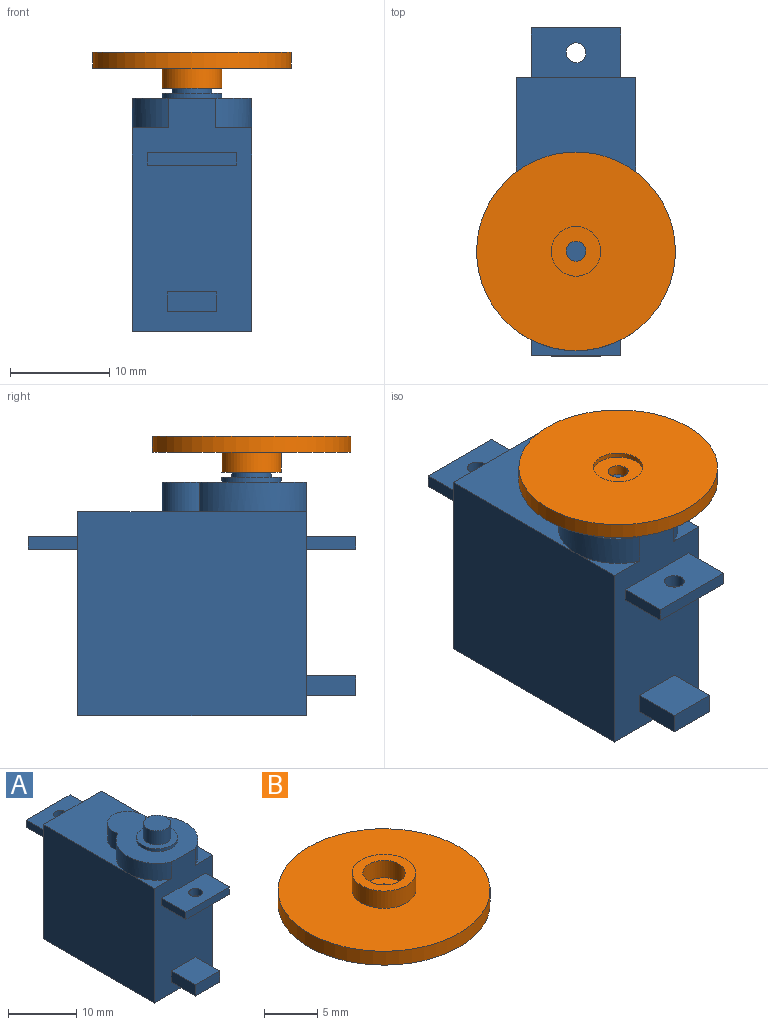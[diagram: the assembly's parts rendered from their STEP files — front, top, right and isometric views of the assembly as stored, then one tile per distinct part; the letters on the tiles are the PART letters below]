
ASSEMBLY  parts=2 mates=1
PART A: 33 faces, bbox 12x33x26.5 mm
  f0: plane 23.5x12mm, normal (0,-1,0), area 238.7mm2, adj f1,f2,f3,f4,f7,f8,f10,f11
  f1: plane 5.5x3.6mm, normal (0,0,1), area 5.5mm2, adj f0,f3,f10
  f2: plane 5.5x3.6mm, normal (0,0,1), area 5.5mm2, adj f0,f4,f8
  f3: plane 23x20.5mm, normal (-1,0,0), area 471.5mm2, adj f0,f1,f5,f6,f7
  f4: plane 23x20.5mm, normal (1,0,0), area 471.5mm2, adj f0,f2,f5,f6,f7
  f5: plane 20.5x12mm, normal (0,1,0), area 234.3mm2, adj f3,f4,f6,f7,f22,f24,f26,f27
  f6: plane 17.5x12mm, normal (0,0,1), area 137.8mm2, adj f3,f4,f5,f8,f9,f10
  f7: plane 23x12mm, normal (0,0,-1), area 276mm2, adj f0,f3,f4,f5
  f8: cylinder r=6mm len=10.75mm, axis (0,0,-1), area 40.1mm2, adj f0,f2,f6,f9,f11
  f9: cylinder r=3mm len=6mm, axis (0,0,-1), area 32.8mm2, adj f6,f8,f10,f11
  f10: cylinder r=6mm len=10.75mm, axis (0,0,-1), area 40.1mm2, adj f0,f1,f6,f9,f11
  f11: plane 14.5x12mm, normal (0,0,1), area 98.9mm2, adj f0,f8,f9,f10,f12
  f12: cylinder r=3mm len=6mm, axis (0,0,-1), area 9.4mm2, adj f11,f13
  f13: plane 6x6mm, normal (0,0,1), area 15.7mm2, adj f12,f14
  f14: cylinder r=2mm len=4mm, axis (0,0,-1), area 31.4mm2, adj f13,f15
  f15: plane 4x4mm, normal (0,0,1), area 12.6mm2, adj f14
  f16: plane 5x1.3mm, normal (-1,0,0), area 6.5mm2, adj f0,f17,f20,f21
  f17: plane 9x1.3mm, normal (0,-1,0), area 11.7mm2, adj f16,f19,f20,f21
  f18: cylinder r=1mm len=2mm, axis (0,0,-1), area 8.2mm2, adj f20,f21
  f19: plane 5x1.3mm, normal (1,0,0), area 6.5mm2, adj f0,f17,f20,f21
  f20: plane 9x5mm, normal (0,0,1), area 41.9mm2, adj f0,f16,f17,f18,f19
  f21: plane 9x5mm, normal (0,0,-1), area 41.9mm2, adj f0,f16,f17,f18,f19
  f22: plane 5x1.3mm, normal (1,0,0), area 6.5mm2, adj f5,f23,f26,f27
  f23: plane 9x1.3mm, normal (0,1,0), area 11.7mm2, adj f22,f24,f26,f27
  f24: plane 5x1.3mm, normal (-1,0,0), area 6.5mm2, adj f5,f23,f26,f27
  f25: cylinder r=1mm len=2mm, axis (0,0,-1), area 8.2mm2, adj f26,f27
  f26: plane 9x5mm, normal (0,0,1), area 41.9mm2, adj f5,f22,f23,f24,f25
  f27: plane 9x5mm, normal (0,0,-1), area 41.9mm2, adj f5,f22,f23,f24,f25
  f28: plane 5x2mm, normal (0,-1,0), area 10mm2, adj f29,f30,f31,f32
  f29: plane 5x2mm, normal (1,0,0), area 10mm2, adj f0,f28,f30,f32
  f30: plane 5x5mm, normal (0,0,1), area 25mm2, adj f0,f28,f29,f31
  f31: plane 5x2mm, normal (-1,0,0), area 10mm2, adj f0,f28,f30,f32
  f32: plane 5x5mm, normal (0,0,-1), area 25mm2, adj f0,f28,f29,f31
PART B: 10 faces, bbox 20x20x3.6 mm
  f0: plane 4x4mm, normal (0,0,1), area 9.4mm2, adj f5,f7
  f1: cylinder r=2.5mm len=5mm, axis (0,0,-1), area 7.9mm2, adj f3,f4
  f2: cylinder r=10mm len=20mm, axis (0,0,-1), area 100.5mm2, adj f3,f6
  f3: plane 20x20mm, normal (0,0,-1), area 294.5mm2, adj f1,f2
  f4: plane 5x5mm, normal (0,0,-1), area 16.5mm2, adj f1,f5
  f5: cylinder r=1mm len=2mm, axis (0,0,-1), area 6.9mm2, adj f0,f4
  f6: plane 20x20mm, normal (0,0,1), area 285.9mm2, adj f2,f8
  f7: cylinder r=2mm len=4mm, axis (0,0,-1), area 25.1mm2, adj f0,f9
  f8: cylinder r=3mm len=6mm, axis (0,0,-1), area 37.7mm2, adj f6,f9
  f9: plane 6x6mm, normal (0,0,1), area 15.7mm2, adj f7,f8
PLACE A at identity
PLACE B rot(axis=(0.71,-0.71,0),180deg) t=(-6.56,8.98,28.1)mm
MATE revolute B.f1 <-> A.f8  axis (0,0,-1) through (-56.64,-57.46,26.5)mm
